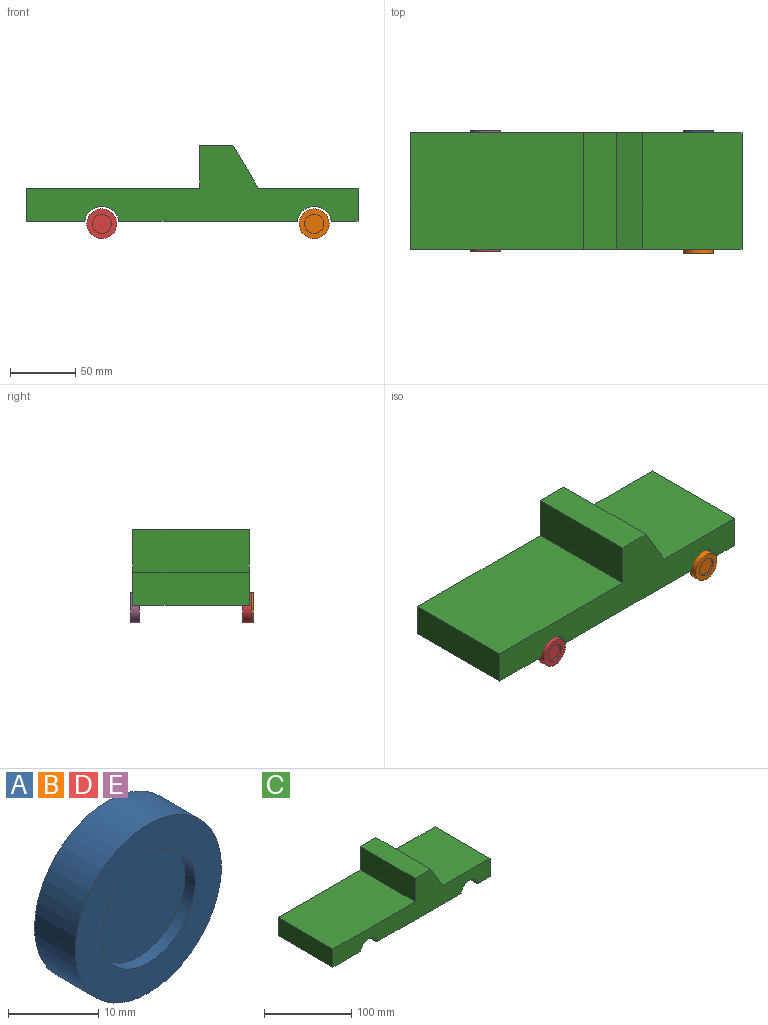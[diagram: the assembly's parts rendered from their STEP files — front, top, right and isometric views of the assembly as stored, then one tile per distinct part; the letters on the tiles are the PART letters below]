
ASSEMBLY  parts=5 mates=4
PART A: 7 faces, bbox 22.9x6.4x22.9 mm
  f0: plane 14.68x14.68mm, normal (0,-1,0), area 169.1mm2, adj f2
  f1: cylinder r=7.34mm len=14.68mm, axis (0,1,0), area 73.2mm2, adj f5,f6
  f2: cylinder r=7.34mm len=14.68mm, axis (0,1,0), area 73.2mm2, adj f0,f4
  f3: cylinder r=11.43mm len=22.86mm, axis (0,1,0), area 456mm2, adj f4,f5
  f4: plane 22.86x22.86mm, normal (0,-1,0), area 241.3mm2, adj f2,f3
  f5: plane 22.86x22.86mm, normal (0,1,0), area 241.3mm2, adj f1,f3
  f6: plane 14.68x14.68mm, normal (0,1,0), area 169.1mm2, adj f1
PART B: same geometry as A
PART C: 14 faces, bbox 254x88.9x58.2 mm
  f0: cylinder r=13.25mm len=88.9mm, axis (0,1,0), area 3365.8mm2, adj f1,f11,f12,f13
  f1: plane 136.24x88.9mm, normal (0,0,-1), area 12111.4mm2, adj f0,f2,f12,f13
  f2: cylinder r=13.25mm len=88.9mm, axis (0,1,0), area 3365.8mm2, adj f1,f3,f12,f13
  f3: plane 88.9x20.4mm, normal (0,0,-1), area 1813.6mm2, adj f2,f4,f12,f13
  f4: plane 88.9x25.4mm, normal (1,0,0), area 2258.1mm2, adj f3,f5,f12,f13
  f5: plane 88.9x76.2mm, normal (0,0,1), area 6774.2mm2, adj f4,f6,f12,f13
  f6: plane 88.9x32.77mm, normal (0.86,0,0.51), area 3387.1mm2, adj f5,f7,f12,f13
  f7: plane 88.9x25.4mm, normal (0,0,1), area 2258.1mm2, adj f6,f8,f12,f13
  f8: plane 88.9x32.77mm, normal (-1,0,0), area 2913.3mm2, adj f7,f9,f12,f13
  f9: plane 132.96x88.9mm, normal (0,0,1), area 11820.6mm2, adj f8,f10,f12,f13
  f10: plane 88.9x25.4mm, normal (-1,0,0), area 2258.1mm2, adj f9,f11,f12,f13
  f11: plane 88.9x44.91mm, normal (0,0,-1), area 3992.6mm2, adj f0,f10,f12,f13
  f12: plane 254x58.17mm, normal (0,-1,0), area 7150mm2, adj f0,f1,f2,f3,f4,f5,f6,f7
  f13: plane 254x58.17mm, normal (0,1,0), area 7150mm2, adj f0,f1,f2,f3,f4,f5,f6,f7
PART D: same geometry as A
PART E: same geometry as A
PLACE A t=(73.13,66.38,-11.39)mm
PLACE B t=(73.13,-20.8,-11.39)mm
PLACE C t=(-88.26,67.97,-9.52)mm
PLACE D t=(-89.34,-19.22,-11.39)mm
PLACE E t=(-89.34,66.38,-11.39)mm
MATE revolute B.f1 <-> A.f3  axis (0,-1,0) through (73.13,-22.39,-11.39)mm
MATE fastened E.f1 <-> C.f0  axis (0,1,0) through (-89.34,67.97,-11.39)mm
MATE fastened A.f1 <-> C.f2  axis (0,1,0) through (73.13,67.97,-11.39)mm
MATE revolute D.f1 <-> E.f1  axis (0,-1,0) through (-89.34,-22.39,-11.39)mm
